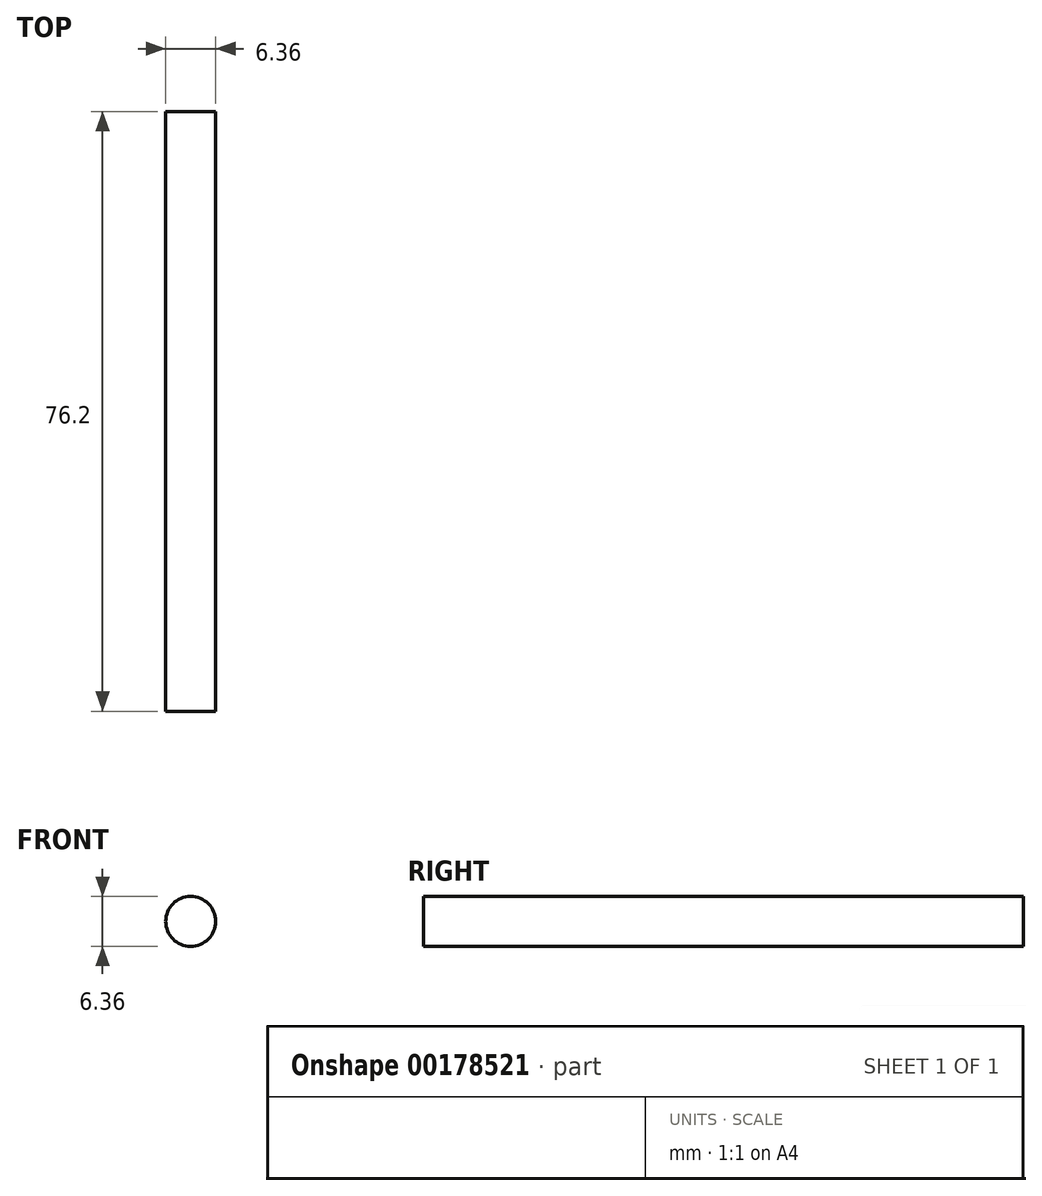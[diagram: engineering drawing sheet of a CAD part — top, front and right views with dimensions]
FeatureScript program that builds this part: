
annotation { "Feature Type Name" : "Feature", "Feature Type Description" : "" }
export const myFeature = defineFeature(function(context is Context, id is Id, definition is map)
    precondition{}
    {
        {
            var Q0;
            Q0=qCreatedBy(makeId("Front.planeOp"),FACE);
            var sketch = newSketch(context, id + "F0", { "sketchPlane" : qUnion([Q0])});
            skCircle(sketch, "E0", {"center": v(0, 0) * mm, "radius": 3.18 * mm});
            skSolve(sketch);
        }
        {
            var Q0;
            Q0=makeQuery(id+"F0.imprint","IMPRINT",FACE,{"disambiguationData":[TD([[makeQuery(id+"F0.imprint","IMPRINT",EDGE,{"derivedFrom":sQuery(id+"F0.wireOp",EDGE,"E0")}),1.0]])]});
            extrude(context, id + "F1", {"entities" : qUnion([Q0]), "depth" : 76.2 * mm});
        }
    });
